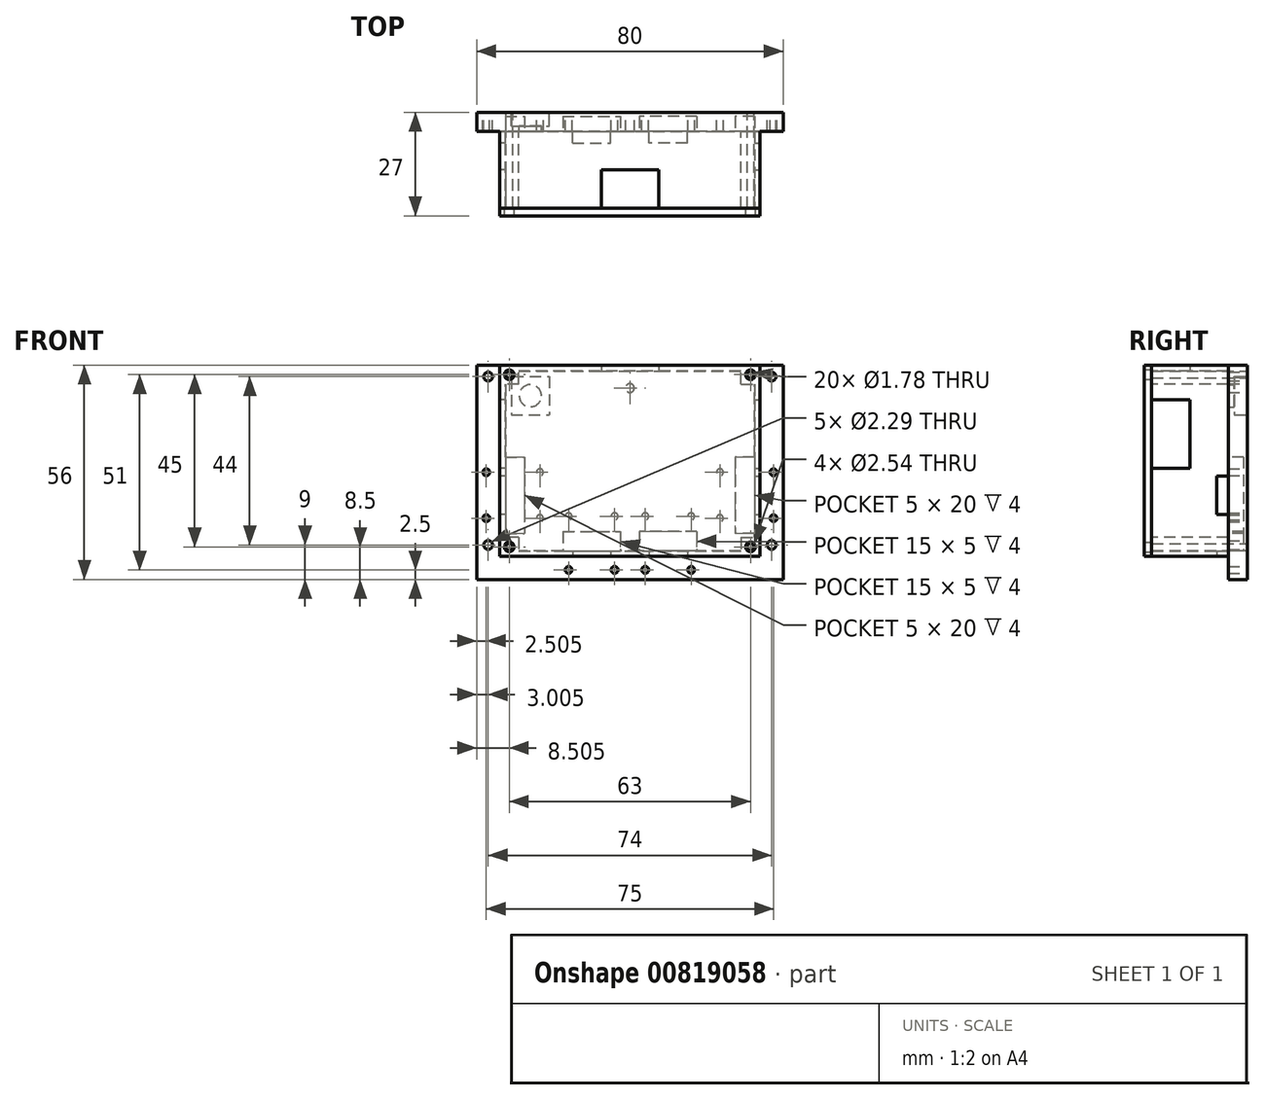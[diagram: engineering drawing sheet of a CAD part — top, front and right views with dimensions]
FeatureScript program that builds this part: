
annotation { "Feature Type Name" : "Feature", "Feature Type Description" : "" }
export const myFeature = defineFeature(function(context is Context, id is Id, definition is map)
    precondition{}
    {
        {
            var Q0;
            Q0=qCreatedBy(makeId("Front.planeOp"),FACE);
            var sketch = newSketch(context, id + "F0", { "sketchPlane" : qUnion([Q0])});
            skCircle(sketch, "E0", {"center": v(-19.88, 15) * mm, "radius": 0.89 * mm});
            skCircle(sketch, "E1", {"center": v(-25.88, -10.5) * mm, "radius": 0.89 * mm});
            skCircle(sketch, "E2", {"center": v(-11.88, -10.5) * mm, "radius": 0.89 * mm});
            skCircle(sketch, "E3", {"center": v(-11.88, -22.5) * mm, "radius": 0.89 * mm});
            skCircle(sketch, "E4", {"center": v(-25.88, -22.5) * mm, "radius": 0.89 * mm});
            skCircle(sketch, "E5", {"center": v(-25.38, -29.5) * mm, "radius": 1.14 * mm});
            skLineSegment(sketch, "E6", {"start": v(51.62, 17.5) * mm, "end": v(-28.38, 17.5) * mm});
            skLineSegment(sketch, "E7", {"start": v(-28.37, 17.5) * mm, "end": v(-28.38, -32.5) * mm});
            skLineSegment(sketch, "E8", {"start": v(51.63, -32.5) * mm, "end": v(-28.38, -32.5) * mm});
            skLineSegment(sketch, "E9.bottom", {"start": v(-28.38, -32.5) * mm, "end": v(-22.38, -32.5) * mm, "construction": true});
            skLineSegment(sketch, "E9.top", {"start": v(-28.38, -26.5) * mm, "end": v(-22.38, -26.5) * mm, "construction": true});
            skLineSegment(sketch, "E9.left", {"start": v(-28.38, -32.5) * mm, "end": v(-28.38, -26.5) * mm, "construction": true});
            skLineSegment(sketch, "E9.right", {"start": v(-22.38, -32.5) * mm, "end": v(-22.38, -26.5) * mm, "construction": true});
            skLineSegment(sketch, "E10", {"start": v(-28.37, -26.5) * mm, "end": v(-22.38, -32.5) * mm});
            skLineSegment(sketch, "E11", {"start": v(-28.38, -32.5) * mm, "end": v(-22.38, -26.5) * mm});
            skPoint(sketch, "E12", {"position": v(-28.38, -7.5) * mm});
            skLineSegment(sketch, "E13", {"start": v(11.62, 17.5) * mm, "end": v(-19.88, 17.5) * mm, "construction": true});
            skLineSegment(sketch, "E14", {"start": v(-19.88, 17.5) * mm, "end": v(-19.88, 15) * mm});
            skLineSegment(sketch, "E15", {"start": v(-11.88, -10.5) * mm, "end": v(-11.88, -22.5) * mm, "construction": true});
            skPoint(sketch, "E16", {"position": v(-11.88, -16.5) * mm});
            skLineSegment(sketch, "E17", {"start": v(-11.88, -16.5) * mm, "end": v(-28.38, -16.5) * mm, "construction": true});
            skLineSegment(sketch, "E18", {"start": v(-25.88, -22.5) * mm, "end": v(-25.88, -10.5) * mm, "construction": true});
            skPoint(sketch, "E19", {"position": v(-25.88, -16.5) * mm});
            skPoint(sketch, "E20", {"position": v(-20.88, -16.5) * mm});
            skLineSegment(sketch, "E21", {"start": v(-20.88, -16.5) * mm, "end": v(-20.88, -6.5) * mm, "construction": true});
            skLineSegment(sketch, "E22", {"start": v(-20.88, -6.5) * mm, "end": v(-15.88, -6.5) * mm, "construction": true});
            skLineSegment(sketch, "E23", {"start": v(-15.88, -6.5) * mm, "end": v(-15.88, -26.5) * mm, "construction": true});
            skLineSegment(sketch, "E24.bottom", {"start": v(-20.88, -6.5) * mm, "end": v(-15.88, -6.5) * mm});
            skLineSegment(sketch, "E24.top", {"start": v(-20.88, -26.5) * mm, "end": v(-15.88, -26.5) * mm});
            skLineSegment(sketch, "E24.left", {"start": v(-20.88, -6.5) * mm, "end": v(-20.88, -26.5) * mm});
            skLineSegment(sketch, "E24.right", {"start": v(-15.88, -6.5) * mm, "end": v(-15.88, -26.5) * mm});
            skLineSegment(sketch, "E25", {"start": v(-25.88, -10.5) * mm, "end": v(-28.38, -10.5) * mm, "construction": true});
            skLineSegment(sketch, "E26", {"start": v(-20.88, -6.5) * mm, "end": v(-28.38, -6.5) * mm, "construction": true});
            skLineSegment(sketch, "E27", {"start": v(51.62, 17.5) * mm, "end": v(51.63, -32.5) * mm});
            skLineSegment(sketch, "E28", {"start": v(11.62, 27.5) * mm, "end": v(11.62, 17.5) * mm, "construction": true});
            skLineSegment(sketch, "E29.bottom", {"start": v(-28.38, 17.5) * mm, "end": v(-22.38, 17.5) * mm, "construction": true});
            skLineSegment(sketch, "E29.top", {"start": v(-28.38, 11.5) * mm, "end": v(-22.38, 11.5) * mm, "construction": true});
            skLineSegment(sketch, "E29.left", {"start": v(-28.38, 17.5) * mm, "end": v(-28.38, 11.5) * mm, "construction": true});
            skLineSegment(sketch, "E29.right", {"start": v(-22.38, 17.5) * mm, "end": v(-22.38, 11.5) * mm, "construction": true});
            skLineSegment(sketch, "E30", {"start": v(-28.38, 17.5) * mm, "end": v(-22.38, 11.5) * mm, "construction": true});
            skLineSegment(sketch, "E31", {"start": v(-28.38, 11.5) * mm, "end": v(-22.38, 17.5) * mm, "construction": true});
            skCircle(sketch, "E32", {"center": v(-25.38, 14.5) * mm, "radius": 1.14 * mm});
            skCircle(sketch, "E33.MirrorC", {"center": v(48.62, -29.5) * mm, "radius": 1.14 * mm});
            skCircle(sketch, "E34.MirrorC", {"center": v(49.13, -22.5) * mm, "radius": 0.89 * mm});
            skLineSegment(sketch, "E35.MirrorCS", {"start": v(39.13, -6.5) * mm, "end": v(39.13, -26.5) * mm});
            skLineSegment(sketch, "E36.MirrorCS", {"start": v(44.13, -6.5) * mm, "end": v(39.13, -6.5) * mm});
            skLineSegment(sketch, "E37.MirrorCS", {"start": v(44.13, -6.5) * mm, "end": v(44.13, -26.5) * mm});
            skPoint(sketch, "E38.MirrorP", {"position": v(44.13, -16.5) * mm});
            skLineSegment(sketch, "E39.MirrorCS", {"start": v(44.13, -6.5) * mm, "end": v(39.13, -6.5) * mm, "construction": true});
            skLineSegment(sketch, "E40.MirrorCS", {"start": v(35.12, -10.5) * mm, "end": v(35.12, -22.5) * mm, "construction": true});
            skLineSegment(sketch, "E41.MirrorCS", {"start": v(44.13, -26.5) * mm, "end": v(39.13, -26.5) * mm});
            skLineSegment(sketch, "E42.MirrorCS", {"start": v(44.13, -16.5) * mm, "end": v(44.13, -6.5) * mm, "construction": true});
            skCircle(sketch, "E43.MirrorC", {"center": v(35.12, -22.5) * mm, "radius": 0.89 * mm});
            skCircle(sketch, "E44.MirrorC", {"center": v(35.12, -10.5) * mm, "radius": 0.89 * mm});
            skPoint(sketch, "E45.MirrorP", {"position": v(49.13, -16.5) * mm});
            skPoint(sketch, "E46.MirrorP", {"position": v(35.12, -16.5) * mm});
            skCircle(sketch, "E47.MirrorC", {"center": v(49.13, -10.5) * mm, "radius": 0.89 * mm});
            skLineSegment(sketch, "E48.MirrorCS", {"start": v(49.12, -22.5) * mm, "end": v(49.12, -10.5) * mm, "construction": true});
            skLineSegment(sketch, "E49.MirrorCS", {"start": v(39.13, -6.5) * mm, "end": v(39.13, -26.5) * mm, "construction": true});
            skPoint(sketch, "E50.MirrorP", {"position": v(51.62, -7.5) * mm});
            skCircle(sketch, "E51.MirrorC", {"center": v(48.62, 14.5) * mm, "radius": 1.14 * mm});
            skCircle(sketch, "E52.MirrorC", {"center": v(43.12, 15) * mm, "radius": 0.89 * mm});
            skLineSegment(sketch, "E53", {"start": v(44.13, -26.5) * mm, "end": v(45.63, -26.5) * mm, "construction": true});
            skLineSegment(sketch, "E54", {"start": v(45.63, -26.5) * mm, "end": v(45.63, -32.5) * mm});
            skLineSegment(sketch, "E55", {"start": v(45.63, -26.5) * mm, "end": v(45.63, 17.5) * mm});
            skLineSegment(sketch, "E56", {"start": v(-20.88, -26.5) * mm, "end": v(-22.38, -26.5) * mm, "construction": true});
            skLineSegment(sketch, "E57.bottom", {"start": v(-22.38, 17.5) * mm, "end": v(45.62, 17.5) * mm});
            skLineSegment(sketch, "E57.top", {"start": v(-22.38, -32.5) * mm, "end": v(45.63, -32.5) * mm});
            skLineSegment(sketch, "E57.left", {"start": v(-22.38, 17.5) * mm, "end": v(-22.38, -32.5) * mm});
            skLineSegment(sketch, "E57.right", {"start": v(45.63, 17.5) * mm, "end": v(45.63, -32.5) * mm});
            skLineSegment(sketch, "E58", {"start": v(-19.88, 15) * mm, "end": v(-17.38, 15) * mm, "construction": true});
            skLineSegment(sketch, "E59", {"start": v(-17.38, 15) * mm, "end": v(-17.38, 12.5) * mm, "construction": true});
            skLineSegment(sketch, "E60.bottom", {"start": v(-17.38, 12.5) * mm, "end": v(-22.38, 12.5) * mm});
            skLineSegment(sketch, "E60.top", {"start": v(-17.38, 17.5) * mm, "end": v(-22.38, 17.5) * mm});
            skLineSegment(sketch, "E60.left", {"start": v(-17.38, 12.5) * mm, "end": v(-17.38, 17.5) * mm});
            skLineSegment(sketch, "E60.right", {"start": v(-22.38, 12.5) * mm, "end": v(-22.38, 17.5) * mm});
            skLineSegment(sketch, "E61", {"start": v(43.12, 15) * mm, "end": v(40.63, 15) * mm, "construction": true});
            skLineSegment(sketch, "E62", {"start": v(40.63, 15) * mm, "end": v(40.63, 12.5) * mm, "construction": true});
            skLineSegment(sketch, "E63.bottom", {"start": v(40.63, 12.5) * mm, "end": v(45.62, 12.5) * mm});
            skLineSegment(sketch, "E63.top", {"start": v(40.63, 17.5) * mm, "end": v(45.62, 17.5) * mm});
            skLineSegment(sketch, "E63.left", {"start": v(40.63, 12.5) * mm, "end": v(40.63, 17.5) * mm});
            skLineSegment(sketch, "E63.right", {"start": v(45.63, 12.5) * mm, "end": v(45.63, 17.5) * mm});
            skLineSegment(sketch, "E64", {"start": v(11.63, -32.5) * mm, "end": v(13.43, -32.5) * mm});
            skLineSegment(sketch, "E65", {"start": v(44.13, -16.5) * mm, "end": v(47.13, -16.5) * mm, "construction": true});
            skLineSegment(sketch, "E66.bottom", {"start": v(43.13, -11.5) * mm, "end": v(47.13, -11.5) * mm});
            skLineSegment(sketch, "E66.top", {"start": v(43.13, -21.5) * mm, "end": v(47.13, -21.5) * mm});
            skLineSegment(sketch, "E66.left", {"start": v(43.13, -11.5) * mm, "end": v(43.13, -21.5) * mm});
            skLineSegment(sketch, "E66.right", {"start": v(47.13, -11.5) * mm, "end": v(47.13, -21.5) * mm});
            skPoint(sketch, "E67", {"position": v(47.13, -16.5) * mm});
            skLineSegment(sketch, "E68.MirrorCS", {"start": v(-19.88, -21.5) * mm, "end": v(-23.88, -21.5) * mm});
            skLineSegment(sketch, "E69.MirrorCS", {"start": v(-19.87, -11.5) * mm, "end": v(-19.87, -21.5) * mm});
            skLineSegment(sketch, "E70.MirrorCS", {"start": v(-23.87, -11.5) * mm, "end": v(-23.87, -21.5) * mm});
            skLineSegment(sketch, "E71.MirrorCS", {"start": v(-19.88, -11.5) * mm, "end": v(-23.88, -11.5) * mm});
            skPoint(sketch, "E72", {"position": v(45.62, 27.5) * mm});
            skLineSegment(sketch, "E73.bottom", {"start": v(4.12, 17.5) * mm, "end": v(19.12, 17.5) * mm});
            skLineSegment(sketch, "E73.top", {"start": v(4.12, 13.5) * mm, "end": v(19.12, 13.5) * mm});
            skLineSegment(sketch, "E73.left", {"start": v(4.12, 17.5) * mm, "end": v(4.12, 13.5) * mm});
            skLineSegment(sketch, "E73.right", {"start": v(19.12, 17.5) * mm, "end": v(19.12, 13.5) * mm});
            skPoint(sketch, "E74", {"position": v(11.62, 17.5) * mm});
            skLineSegment(sketch, "E75", {"start": v(-22.38, 17.5) * mm, "end": v(-19.88, 17.5) * mm});
            skLineSegment(sketch, "E76", {"start": v(-5.88, -32.5) * mm, "end": v(-5.88, -31) * mm, "construction": true});
            skLineSegment(sketch, "E77.bottom", {"start": v(-5.88, -26) * mm, "end": v(9.12, -26) * mm});
            skLineSegment(sketch, "E77.top", {"start": v(-5.88, -31) * mm, "end": v(9.12, -31) * mm});
            skLineSegment(sketch, "E77.left", {"start": v(-5.88, -26) * mm, "end": v(-5.88, -31) * mm});
            skLineSegment(sketch, "E77.right", {"start": v(9.12, -26) * mm, "end": v(9.12, -31) * mm});
            skPoint(sketch, "E78", {"position": v(1.62, -26) * mm});
            skLineSegment(sketch, "E79", {"start": v(1.62, -26) * mm, "end": v(1.62, -22) * mm, "construction": true});
            skLineSegment(sketch, "E80", {"start": v(-4.38, -22) * mm, "end": v(7.63, -22) * mm, "construction": true});
            skPoint(sketch, "E81", {"position": v(1.62, -22) * mm});
            skCircle(sketch, "E82", {"center": v(-4.38, -22) * mm, "radius": 0.89 * mm});
            skCircle(sketch, "E83", {"center": v(7.63, -22) * mm, "radius": 0.89 * mm});
            skLineSegment(sketch, "E84.bottom", {"start": v(-28.37, -32.5) * mm, "end": v(51.63, -32.5) * mm});
            skLineSegment(sketch, "E84.top", {"start": v(-28.37, -38.5) * mm, "end": v(51.63, -38.5) * mm});
            skLineSegment(sketch, "E84.left", {"start": v(-28.38, -32.5) * mm, "end": v(-28.38, -38.5) * mm});
            skLineSegment(sketch, "E84.right", {"start": v(51.63, -32.5) * mm, "end": v(51.63, -38.5) * mm});
            skLineSegment(sketch, "E85.bottom", {"start": v(-3.37, -31) * mm, "end": v(6.63, -31) * mm});
            skLineSegment(sketch, "E85.top", {"start": v(-3.38, -34) * mm, "end": v(6.63, -34) * mm});
            skLineSegment(sketch, "E85.left", {"start": v(-3.38, -31) * mm, "end": v(-3.38, -34) * mm});
            skLineSegment(sketch, "E85.right", {"start": v(6.63, -31) * mm, "end": v(6.63, -34) * mm});
            skPoint(sketch, "E86", {"position": v(1.63, -31) * mm});
            skPoint(sketch, "E87", {"position": v(1.62, -31) * mm});
            skLineSegment(sketch, "E88", {"start": v(1.63, -31) * mm, "end": v(1.63, -38.5) * mm, "construction": true});
            skLineSegment(sketch, "E89", {"start": v(1.63, -38.5) * mm, "end": v(1.63, -36) * mm, "construction": true});
            skLineSegment(sketch, "E90", {"start": v(-4.38, -36) * mm, "end": v(7.63, -36) * mm, "construction": true});
            skPoint(sketch, "E91", {"position": v(1.62, -36) * mm});
            skCircle(sketch, "E92", {"center": v(-4.38, -36) * mm, "radius": 0.89 * mm});
            skCircle(sketch, "E93", {"center": v(7.63, -36) * mm, "radius": 0.89 * mm});
            skCircle(sketch, "E94.MirrorC", {"center": v(15.62, -36) * mm, "radius": 0.89 * mm});
            skCircle(sketch, "E95.MirrorC", {"center": v(27.63, -36) * mm, "radius": 0.89 * mm});
            skLineSegment(sketch, "E96.MirrorCS", {"start": v(21.62, -38.5) * mm, "end": v(21.62, -36) * mm, "construction": true});
            skLineSegment(sketch, "E97.MirrorCS", {"start": v(26.62, -31) * mm, "end": v(26.62, -34) * mm});
            skLineSegment(sketch, "E98.MirrorCS", {"start": v(29.12, -32.5) * mm, "end": v(29.12, -31) * mm, "construction": true});
            skLineSegment(sketch, "E99.MirrorCS", {"start": v(29.12, -31) * mm, "end": v(14.12, -31) * mm});
            skPoint(sketch, "E100.MirrorP", {"position": v(21.62, -31) * mm});
            skLineSegment(sketch, "E101.MirrorCS", {"start": v(11.62, -32.5) * mm, "end": v(9.82, -32.5) * mm});
            skCircle(sketch, "E102.MirrorC", {"center": v(27.63, -22) * mm, "radius": 0.89 * mm});
            skCircle(sketch, "E103.MirrorC", {"center": v(15.62, -22) * mm, "radius": 0.89 * mm});
            skPoint(sketch, "E104.MirrorP", {"position": v(21.62, -36) * mm});
            skPoint(sketch, "E105.MirrorP", {"position": v(21.63, -31) * mm});
            skPoint(sketch, "E106.MirrorP", {"position": v(21.63, -26) * mm});
            skLineSegment(sketch, "E107.MirrorCS", {"start": v(21.63, -26) * mm, "end": v(21.63, -22) * mm, "construction": true});
            skLineSegment(sketch, "E108.MirrorCS", {"start": v(29.12, -26) * mm, "end": v(29.12, -31) * mm});
            skLineSegment(sketch, "E109.MirrorCS", {"start": v(27.63, -36) * mm, "end": v(15.62, -36) * mm, "construction": true});
            skLineSegment(sketch, "E110.MirrorCS", {"start": v(26.62, -34) * mm, "end": v(16.62, -34) * mm});
            skLineSegment(sketch, "E111.MirrorCS", {"start": v(21.62, -31) * mm, "end": v(21.62, -38.5) * mm, "construction": true});
            skLineSegment(sketch, "E112.MirrorCS", {"start": v(27.63, -22) * mm, "end": v(15.62, -22) * mm, "construction": true});
            skLineSegment(sketch, "E113.MirrorCS", {"start": v(29.12, -26) * mm, "end": v(14.12, -26) * mm});
            skLineSegment(sketch, "E114.MirrorCS", {"start": v(16.62, -31) * mm, "end": v(16.62, -34) * mm});
            skPoint(sketch, "E115.MirrorP", {"position": v(21.63, -22) * mm});
            skLineSegment(sketch, "E116.MirrorCS", {"start": v(26.62, -31) * mm, "end": v(16.62, -31) * mm});
            skLineSegment(sketch, "E117.MirrorCS", {"start": v(14.12, -26) * mm, "end": v(14.12, -31) * mm});
            skLineSegment(sketch, "E118", {"start": v(-28.38, -7.5) * mm, "end": v(51.62, -7.5) * mm, "construction": true});
            skCircle(sketch, "E119.MirrorC", {"center": v(43.13, -30) * mm, "radius": 0.89 * mm});
            skLineSegment(sketch, "E120.MirrorCS", {"start": v(40.63, -27.5) * mm, "end": v(45.63, -27.5) * mm});
            skLineSegment(sketch, "E121.MirrorCS", {"start": v(45.63, -27.5) * mm, "end": v(45.63, -32.5) * mm});
            skLineSegment(sketch, "E122.MirrorCS", {"start": v(40.63, -27.5) * mm, "end": v(40.63, -32.5) * mm});
            skLineSegment(sketch, "E123.MirrorCS", {"start": v(40.63, -32.5) * mm, "end": v(45.62, -32.5) * mm});
            skLineSegment(sketch, "E124.MirrorCS", {"start": v(40.63, -30) * mm, "end": v(40.63, -27.5) * mm, "construction": true});
            skLineSegment(sketch, "E125.MirrorCS", {"start": v(43.13, -30) * mm, "end": v(40.63, -30) * mm, "construction": true});
            skLineSegment(sketch, "E126.MirrorCS", {"start": v(-17.37, -27.5) * mm, "end": v(-17.37, -32.5) * mm});
            skLineSegment(sketch, "E127.MirrorCS", {"start": v(-19.88, -30) * mm, "end": v(-17.37, -30) * mm, "construction": true});
            skLineSegment(sketch, "E128.MirrorCS", {"start": v(-17.37, -30) * mm, "end": v(-17.37, -27.5) * mm, "construction": true});
            skLineSegment(sketch, "E129.MirrorCS", {"start": v(-17.38, -27.5) * mm, "end": v(-22.37, -27.5) * mm});
            skCircle(sketch, "E130.MirrorC", {"center": v(-19.88, -30) * mm, "radius": 0.89 * mm});
            skLineSegment(sketch, "E131.MirrorCS", {"start": v(-17.37, -32.5) * mm, "end": v(-22.38, -32.5) * mm});
            skLineSegment(sketch, "E132.MirrorCS", {"start": v(-22.38, -32.5) * mm, "end": v(-19.88, -32.5) * mm});
            skLineSegment(sketch, "E133.MirrorCS", {"start": v(-19.88, -32.5) * mm, "end": v(-19.88, -30) * mm});
            skLineSegment(sketch, "E134.MirrorCS", {"start": v(-22.38, -27.5) * mm, "end": v(-22.38, -32.5) * mm});
            skLineSegment(sketch, "E135.bottom", {"start": v(41.62, 8.5) * mm, "end": v(45.62, 8.5) * mm});
            skLineSegment(sketch, "E135.top", {"start": v(41.62, -9.5) * mm, "end": v(45.62, -9.5) * mm});
            skLineSegment(sketch, "E135.left", {"start": v(41.62, 8.5) * mm, "end": v(41.62, -9.5) * mm});
            skLineSegment(sketch, "E135.right", {"start": v(45.62, 8.5) * mm, "end": v(45.62, -9.5) * mm});
            skPoint(sketch, "E136", {"position": v(45.62, -0.5) * mm});
            skPoint(sketch, "E137.MirrorP", {"position": v(-22.38, -0.5) * mm});
            skLineSegment(sketch, "E138.MirrorCS", {"start": v(-22.38, 8.5) * mm, "end": v(-22.38, -9.5) * mm});
            skLineSegment(sketch, "E139.MirrorCS", {"start": v(-18.38, 8.5) * mm, "end": v(-18.38, -9.5) * mm});
            skLineSegment(sketch, "E140.MirrorCS", {"start": v(-18.38, 8.5) * mm, "end": v(-22.38, 8.5) * mm});
            skLineSegment(sketch, "E141.MirrorCS", {"start": v(-18.38, -9.5) * mm, "end": v(-22.38, -9.5) * mm});
            skCircle(sketch, "E142", {"center": v(-14.38, 9.5) * mm, "radius": 2.9 * mm, "construction": true});
            skLineSegment(sketch, "E143", {"start": v(-14.38, 9.5) * mm, "end": v(-14.38, 14.5) * mm, "construction": true});
            skLineSegment(sketch, "E144", {"start": v(-14.38, 14.5) * mm, "end": v(-19.38, 14.5) * mm, "construction": true});
            skLineSegment(sketch, "E145.bottom", {"start": v(-19.38, 14.5) * mm, "end": v(-9.38, 14.5) * mm});
            skLineSegment(sketch, "E145.top", {"start": v(-19.38, 4.5) * mm, "end": v(-9.38, 4.5) * mm});
            skLineSegment(sketch, "E145.left", {"start": v(-19.38, 14.5) * mm, "end": v(-19.38, 4.5) * mm});
            skLineSegment(sketch, "E145.right", {"start": v(-9.38, 14.5) * mm, "end": v(-9.38, 4.5) * mm});
            skLineSegment(sketch, "E146", {"start": v(45.62, -0.5) * mm, "end": v(45.62, 17.5) * mm, "construction": true});
            skLineSegment(sketch, "E147", {"start": v(-22.38, 9.5) * mm, "end": v(-14.38, 9.5) * mm, "construction": true});
            skLineSegment(sketch, "E148", {"start": v(-14.38, 17.5) * mm, "end": v(-14.38, 9.5) * mm, "construction": true});
            skLineSegment(sketch, "E149", {"start": v(11.62, 17.5) * mm, "end": v(11.62, 11.5) * mm, "construction": true});
            skCircle(sketch, "E150", {"center": v(11.62, 11.5) * mm, "radius": 1.14 * mm});
            skSolve(sketch);
        }
        {
            var Q0;
            Q0=qCreatedBy(makeId("Front.planeOp"),FACE);
            var sketch = newSketch(context, id + "F1", { "sketchPlane" : qUnion([Q0])});
            skLineSegment(sketch, "E151.0", {"start": v(51.62, 17.5) * mm, "end": v(-28.38, 17.5) * mm});
            skLineSegment(sketch, "E151.1", {"start": v(-28.37, 17.5) * mm, "end": v(-28.38, -32.5) * mm});
            skLineSegment(sketch, "E151.2", {"start": v(51.62, 17.5) * mm, "end": v(51.63, -32.5) * mm});
            skLineSegment(sketch, "E152.0", {"start": v(-28.38, -32.5) * mm, "end": v(-28.38, -38.5) * mm});
            skLineSegment(sketch, "E152.1", {"start": v(-28.37, -38.5) * mm, "end": v(51.63, -38.5) * mm});
            skLineSegment(sketch, "E152.2", {"start": v(51.63, -32.5) * mm, "end": v(51.63, -38.5) * mm});
            skSolve(sketch);
        }
        {
            var Q0;
            Q0=qCreatedBy(makeId("Front.planeOp"),FACE);
            var sketch = newSketch(context, id + "F2", { "sketchPlane" : qUnion([Q0])});
            skLineSegment(sketch, "E153.4", {"start": v(-20.88, -6.5) * mm, "end": v(-15.88, -6.5) * mm});
            skLineSegment(sketch, "E153.5", {"start": v(-20.88, -6.5) * mm, "end": v(-20.88, -26.5) * mm});
            skLineSegment(sketch, "E153.6", {"start": v(-15.88, -6.5) * mm, "end": v(-15.88, -26.5) * mm});
            skLineSegment(sketch, "E153.7", {"start": v(-20.88, -26.5) * mm, "end": v(-15.88, -26.5) * mm});
            skLineSegment(sketch, "E154.5", {"start": v(44.13, -6.5) * mm, "end": v(44.13, -26.5) * mm});
            skLineSegment(sketch, "E154.6", {"start": v(44.13, -6.5) * mm, "end": v(39.13, -6.5) * mm});
            skLineSegment(sketch, "E154.7", {"start": v(39.13, -6.5) * mm, "end": v(39.13, -26.5) * mm});
            skLineSegment(sketch, "E154.8", {"start": v(44.13, -26.5) * mm, "end": v(39.13, -26.5) * mm});
            skLineSegment(sketch, "E155.0", {"start": v(-5.88, -26) * mm, "end": v(9.12, -26) * mm});
            skLineSegment(sketch, "E155.1", {"start": v(-5.88, -26) * mm, "end": v(-5.88, -31) * mm});
            skLineSegment(sketch, "E155.2", {"start": v(-5.88, -31) * mm, "end": v(9.12, -31) * mm});
            skLineSegment(sketch, "E155.3", {"start": v(9.12, -26) * mm, "end": v(9.12, -31) * mm});
            skLineSegment(sketch, "E156.0", {"start": v(29.12, -26) * mm, "end": v(14.12, -26) * mm});
            skLineSegment(sketch, "E156.1", {"start": v(14.12, -26) * mm, "end": v(14.12, -31) * mm});
            skLineSegment(sketch, "E156.2", {"start": v(29.12, -31) * mm, "end": v(14.12, -31) * mm});
            skLineSegment(sketch, "E156.3", {"start": v(29.12, -26) * mm, "end": v(29.12, -31) * mm});
            skSolve(sketch);
        }
        {
            var Q0;
            Q0=qCreatedBy(makeId("Front.planeOp"),FACE);
            var sketch = newSketch(context, id + "F3", { "sketchPlane" : qUnion([Q0])});
            skCircle(sketch, "E157.10", {"center": v(-11.88, -10.5) * mm, "radius": 0.89 * mm});
            skCircle(sketch, "E157.11", {"center": v(-25.88, -10.5) * mm, "radius": 0.89 * mm});
            skCircle(sketch, "E157.12", {"center": v(-25.88, -22.5) * mm, "radius": 0.89 * mm});
            skCircle(sketch, "E157.13", {"center": v(-11.88, -22.5) * mm, "radius": 0.89 * mm});
            skCircle(sketch, "E157.22", {"center": v(-25.38, -29.5) * mm, "radius": 1.14 * mm});
            skCircle(sketch, "E158.0", {"center": v(-25.38, 14.5) * mm, "radius": 1.14 * mm});
            skCircle(sketch, "E158.4", {"center": v(48.62, 14.5) * mm, "radius": 1.14 * mm});
            skCircle(sketch, "E158.5", {"center": v(35.12, -10.5) * mm, "radius": 0.89 * mm});
            skCircle(sketch, "E158.6", {"center": v(35.12, -22.5) * mm, "radius": 0.89 * mm});
            skCircle(sketch, "E158.7", {"center": v(49.13, -10.5) * mm, "radius": 0.89 * mm});
            skCircle(sketch, "E158.8", {"center": v(49.13, -22.5) * mm, "radius": 0.89 * mm});
            skCircle(sketch, "E158.9", {"center": v(48.62, -29.5) * mm, "radius": 1.14 * mm});
            skCircle(sketch, "E159.0", {"center": v(-19.88, 15) * mm, "radius": 0.89 * mm});
            skCircle(sketch, "E159.1", {"center": v(43.12, 15) * mm, "radius": 0.89 * mm});
            skCircle(sketch, "E160.0", {"center": v(-19.88, -30) * mm, "radius": 0.89 * mm});
            skCircle(sketch, "E160.1", {"center": v(-4.38, -22) * mm, "radius": 0.89 * mm});
            skCircle(sketch, "E160.2", {"center": v(7.63, -22) * mm, "radius": 0.89 * mm});
            skCircle(sketch, "E160.3", {"center": v(-4.38, -36) * mm, "radius": 0.89 * mm});
            skCircle(sketch, "E160.4", {"center": v(7.63, -36) * mm, "radius": 0.89 * mm});
            skCircle(sketch, "E160.5", {"center": v(15.62, -22) * mm, "radius": 0.89 * mm});
            skCircle(sketch, "E160.6", {"center": v(27.63, -22) * mm, "radius": 0.89 * mm});
            skCircle(sketch, "E160.7", {"center": v(27.63, -36) * mm, "radius": 0.89 * mm});
            skCircle(sketch, "E160.8", {"center": v(15.62, -36) * mm, "radius": 0.89 * mm});
            skCircle(sketch, "E161.0", {"center": v(43.13, -30) * mm, "radius": 0.89 * mm});
            skCircle(sketch, "E162.0", {"center": v(-14.38, 9.5) * mm, "radius": 2.9 * mm});
            skCircle(sketch, "E163.0", {"center": v(11.62, 11.5) * mm, "radius": 1.14 * mm});
            skSolve(sketch);
        }
        {
            var Q0;
            Q0=qSketchRegion(id+"F1",true);
            extrude(context, id + "F4", {"entities" : qUnion([Q0]), "depth" : 5 * mm, "offsetDistance" : 25 * mm});
        }
        {
            var Q0;
            Q0=qCreatedBy(makeId("Front.planeOp"),FACE);
            var sketch = newSketch(context, id + "F5", { "sketchPlane" : qUnion([Q0])});
            skLineSegment(sketch, "E164.0", {"start": v(-22.38, 17.5) * mm, "end": v(-22.38, -32.5) * mm});
            skLineSegment(sketch, "E164.1", {"start": v(-22.38, 17.5) * mm, "end": v(45.62, 17.5) * mm});
            skLineSegment(sketch, "E164.2", {"start": v(45.63, -26.5) * mm, "end": v(45.63, 17.5) * mm});
            skLineSegment(sketch, "E164.4", {"start": v(45.63, 17.5) * mm, "end": v(45.63, -32.5) * mm});
            skLineSegment(sketch, "E165.0", {"start": v(-22.38, -32.5) * mm, "end": v(45.63, -32.5) * mm});
            skLineSegment(sketch, "E166.0", {"start": v(-20.88, 16) * mm, "end": v(44.13, 16) * mm});
            skLineSegment(sketch, "E166.1", {"start": v(-20.88, 16) * mm, "end": v(-20.88, -31) * mm});
            skLineSegment(sketch, "E166.2", {"start": v(-20.88, -31) * mm, "end": v(44.13, -31) * mm});
            skLineSegment(sketch, "E166.3", {"start": v(44.13, 16) * mm, "end": v(44.13, -31) * mm});
            skSolve(sketch);
        }
        {
            var Q0;
            Q0=qCreatedBy(makeId("Front.planeOp"),FACE);
            var sketch = newSketch(context, id + "F6", { "sketchPlane" : qUnion([Q0])});
            skLineSegment(sketch, "E167.0", {"start": v(-17.38, 12.5) * mm, "end": v(-17.38, 17.5) * mm});
            skLineSegment(sketch, "E167.1", {"start": v(-17.38, 12.5) * mm, "end": v(-22.38, 12.5) * mm});
            skLineSegment(sketch, "E167.2", {"start": v(-17.38, 17.5) * mm, "end": v(-22.38, 17.5) * mm});
            skLineSegment(sketch, "E167.3", {"start": v(-22.38, 12.5) * mm, "end": v(-22.38, 17.5) * mm});
            skLineSegment(sketch, "E168.0", {"start": v(40.63, 12.5) * mm, "end": v(45.62, 12.5) * mm});
            skLineSegment(sketch, "E168.1", {"start": v(40.63, 12.5) * mm, "end": v(40.63, 17.5) * mm});
            skLineSegment(sketch, "E168.2", {"start": v(45.63, 12.5) * mm, "end": v(45.63, 17.5) * mm});
            skLineSegment(sketch, "E168.3", {"start": v(40.63, 17.5) * mm, "end": v(45.62, 17.5) * mm});
            skLineSegment(sketch, "E169.0", {"start": v(-17.38, -27.5) * mm, "end": v(-22.37, -27.5) * mm});
            skLineSegment(sketch, "E169.1", {"start": v(-17.37, -27.5) * mm, "end": v(-17.37, -32.5) * mm});
            skLineSegment(sketch, "E169.2", {"start": v(-17.37, -32.5) * mm, "end": v(-22.38, -32.5) * mm});
            skLineSegment(sketch, "E169.3", {"start": v(-22.38, -27.5) * mm, "end": v(-22.38, -32.5) * mm});
            skPoint(sketch, "E169.4", {"position": v(-19.87, -27.5) * mm});
            skLineSegment(sketch, "E170.0", {"start": v(40.63, -27.5) * mm, "end": v(45.63, -27.5) * mm});
            skLineSegment(sketch, "E170.1", {"start": v(40.63, -27.5) * mm, "end": v(40.63, -32.5) * mm});
            skLineSegment(sketch, "E170.2", {"start": v(45.63, -27.5) * mm, "end": v(45.63, -32.5) * mm});
            skLineSegment(sketch, "E170.3", {"start": v(40.63, -32.5) * mm, "end": v(45.62, -32.5) * mm});
            skSolve(sketch);
        }
        {
            var Q0;
            Q0=qSketchRegion(id+"F5",true);
            extrude(context, id + "F7", {"entities" : qUnion([Q0]), "operationType" : NewBodyOperationType.ADD, "depth" : 25 * mm, "offsetDistance" : 25 * mm});
        }
        {
            var Q0;
            {var subQ0=sQuery(id+"F1.wireOp",EDGE,"E152.2");var subQ1=sQuery(id+"F1.wireOp",EDGE,"E151.2");var subQ2=sQuery(id+"F1.wireOp",EDGE,"E152.0");var subQ3=sQuery(id+"F1.wireOp",EDGE,"E151.1");var subQ4=sQuery(id+"F1.wireOp",EDGE,"E152.1");var subQ5=sQuery(id+"F1.wireOp",EDGE,"E151.0");Q0=makeQuery(id+"F7.boolean.opBoolean","SPLIT",FACE,{"disambiguationData":[TD([makeQuery(id+"F4.opExtrude","SWEPT_FACE",FACE,{"disambiguationData":[OSD([subQ5])]})])],"derivedFrom":makeQuery(id+"F4.opExtrude","CAP_FACE",FACE,{"disambiguationData":[OSD([subQ5,subQ3,subQ1,subQ2,subQ4,subQ0])],"isStart":false})});}
            var sketch = newSketch(context, id + "F8", { "sketchPlane" : qUnion([Q0])});
            skLineSegment(sketch, "E171.0", {"start": v(-20.88, -6.5) * mm, "end": v(-15.88, -6.5) * mm});
            skLineSegment(sketch, "E171.1", {"start": v(-15.88, -6.5) * mm, "end": v(-15.88, -26.5) * mm});
            skLineSegment(sketch, "E171.2", {"start": v(-20.88, -6.5) * mm, "end": v(-20.88, -26.5) * mm});
            skLineSegment(sketch, "E171.3", {"start": v(-20.88, -26.5) * mm, "end": v(-15.88, -26.5) * mm});
            skLineSegment(sketch, "E171.4", {"start": v(-5.88, -26) * mm, "end": v(9.12, -26) * mm});
            skLineSegment(sketch, "E171.5", {"start": v(-5.88, -26) * mm, "end": v(-5.88, -31) * mm});
            skLineSegment(sketch, "E171.6", {"start": v(-5.88, -31) * mm, "end": v(9.12, -31) * mm});
            skLineSegment(sketch, "E171.7", {"start": v(9.12, -26) * mm, "end": v(9.12, -31) * mm});
            skLineSegment(sketch, "E171.8", {"start": v(29.12, -26) * mm, "end": v(14.12, -26) * mm});
            skLineSegment(sketch, "E171.9", {"start": v(14.12, -26) * mm, "end": v(14.12, -31) * mm});
            skLineSegment(sketch, "E171.10", {"start": v(29.12, -31) * mm, "end": v(14.12, -31) * mm});
            skLineSegment(sketch, "E171.11", {"start": v(29.12, -26) * mm, "end": v(29.12, -31) * mm});
            skLineSegment(sketch, "E171.12", {"start": v(39.13, -6.5) * mm, "end": v(39.13, -26.5) * mm});
            skLineSegment(sketch, "E171.13", {"start": v(44.13, -6.5) * mm, "end": v(39.13, -6.5) * mm});
            skLineSegment(sketch, "E171.14", {"start": v(44.13, -26.5) * mm, "end": v(39.13, -26.5) * mm});
            skLineSegment(sketch, "E171.15", {"start": v(44.13, -6.5) * mm, "end": v(44.13, -26.5) * mm});
            skPoint(sketch, "E171.16", {"position": v(41.63, -6.5) * mm});
            skSolve(sketch);
        }
        {
            var Q0;
            Q0=qSketchRegion(id+"F8",true);
            extrude(context, id + "F9", {"entities" : qUnion([Q0]), "operationType" : NewBodyOperationType.REMOVE, "oppositeDirection" : true, "depth" : 4 * mm, "offsetDistance" : 25 * mm});
        }
        {
            var Q0;
            Q0=qSketchRegion(id+"F6",true);
            extrude(context, id + "F10", {"entities" : qUnion([Q0]), "operationType" : NewBodyOperationType.ADD, "depth" : 25 * mm, "offsetDistance" : 25 * mm});
        }
        {
            var Q0;
            {var subQ0=sQuery(id+"F1.wireOp",EDGE,"E152.2");var subQ1=sQuery(id+"F1.wireOp",EDGE,"E151.2");var subQ2=sQuery(id+"F1.wireOp",EDGE,"E152.0");var subQ3=sQuery(id+"F1.wireOp",EDGE,"E151.1");var subQ4=sQuery(id+"F1.wireOp",EDGE,"E152.1");var subQ5=sQuery(id+"F1.wireOp",EDGE,"E151.0");Q0=makeQuery(id+"F7.boolean.opBoolean","SPLIT",FACE,{"disambiguationData":[TD([makeQuery(id+"F4.opExtrude","SWEPT_FACE",FACE,{"disambiguationData":[OSD([subQ5])]})])],"derivedFrom":makeQuery(id+"F4.opExtrude","CAP_FACE",FACE,{"disambiguationData":[OSD([subQ5,subQ3,subQ1,subQ2,subQ4,subQ0])],"isStart":false})});}
            var sketch = newSketch(context, id + "F11", { "sketchPlane" : qUnion([Q0])});
            skLineSegment(sketch, "E172.0", {"start": v(-19.88, -11.5) * mm, "end": v(-23.88, -11.5) * mm});
            skLineSegment(sketch, "E172.1", {"start": v(-23.87, -11.5) * mm, "end": v(-23.87, -21.5) * mm});
            skLineSegment(sketch, "E172.2", {"start": v(-19.87, -11.5) * mm, "end": v(-19.87, -21.5) * mm});
            skLineSegment(sketch, "E172.3", {"start": v(-19.88, -21.5) * mm, "end": v(-23.88, -21.5) * mm});
            skLineSegment(sketch, "E172.4", {"start": v(43.13, -11.5) * mm, "end": v(47.13, -11.5) * mm});
            skLineSegment(sketch, "E172.5", {"start": v(43.13, -11.5) * mm, "end": v(43.13, -21.5) * mm});
            skLineSegment(sketch, "E172.6", {"start": v(47.13, -11.5) * mm, "end": v(47.13, -21.5) * mm});
            skLineSegment(sketch, "E172.7", {"start": v(43.13, -21.5) * mm, "end": v(47.13, -21.5) * mm});
            skLineSegment(sketch, "E173.0", {"start": v(26.62, -34) * mm, "end": v(16.62, -34) * mm});
            skLineSegment(sketch, "E173.1", {"start": v(16.62, -31) * mm, "end": v(16.62, -34) * mm});
            skLineSegment(sketch, "E173.2", {"start": v(26.62, -31) * mm, "end": v(26.62, -34) * mm});
            skLineSegment(sketch, "E174.0", {"start": v(26.62, -31) * mm, "end": v(16.62, -31) * mm});
            skLineSegment(sketch, "E175.0", {"start": v(6.63, -31) * mm, "end": v(6.63, -34) * mm});
            skLineSegment(sketch, "E175.1", {"start": v(-3.38, -31) * mm, "end": v(-3.38, -34) * mm});
            skLineSegment(sketch, "E175.2", {"start": v(-3.38, -34) * mm, "end": v(6.63, -34) * mm});
            skLineSegment(sketch, "E175.3", {"start": v(-3.37, -31) * mm, "end": v(6.63, -31) * mm});
            skSolve(sketch);
        }
        {
            var Q0;
            Q0=qSketchRegion(id+"F11",true);
            extrude(context, id + "F12", {"entities" : qUnion([Q0]), "operationType" : NewBodyOperationType.REMOVE, "depth" : 3 * mm, "offsetDistance" : 25 * mm});
        }
        {
            var Q0;
            Q0=makeQuery(id+"F10.boolean.opBoolean","MERGE",FACE,{"derivedFrom":[makeQuery(id+"F7.opExtrude","CAP_FACE",FACE,{"disambiguationData":[OSD([sQuery(id+"F5.wireOp",EDGE,"E164.0"),sQuery(id+"F5.wireOp",EDGE,"E164.1"),sQuery(id+"F5.wireOp",EDGE,"E164.4"),sQuery(id+"F5.wireOp",EDGE,"E165.0"),sQuery(id+"F5.wireOp",EDGE,"E166.0"),sQuery(id+"F5.wireOp",EDGE,"E166.1"),sQuery(id+"F5.wireOp",EDGE,"E166.2"),sQuery(id+"F5.wireOp",EDGE,"E166.3")])],"isStart":false}),makeQuery(id+"F10.opExtrude","CAP_FACE",FACE,{"disambiguationData":[OSD([sQuery(id+"F6.wireOp",EDGE,"E167.0"),sQuery(id+"F6.wireOp",EDGE,"E167.1"),sQuery(id+"F6.wireOp",EDGE,"E167.2"),sQuery(id+"F6.wireOp",EDGE,"E167.3")])],"isStart":false}),makeQuery(id+"F10.opExtrude","CAP_FACE",FACE,{"disambiguationData":[OSD([sQuery(id+"F6.wireOp",EDGE,"E168.0"),sQuery(id+"F6.wireOp",EDGE,"E168.1"),sQuery(id+"F6.wireOp",EDGE,"E168.2"),sQuery(id+"F6.wireOp",EDGE,"E168.3")])],"isStart":false}),makeQuery(id+"F10.opExtrude","CAP_FACE",FACE,{"disambiguationData":[OSD([sQuery(id+"F6.wireOp",EDGE,"E169.0"),sQuery(id+"F6.wireOp",EDGE,"E169.1"),sQuery(id+"F6.wireOp",EDGE,"E169.2"),sQuery(id+"F6.wireOp",EDGE,"E169.3")])],"isStart":false}),makeQuery(id+"F10.opExtrude","CAP_FACE",FACE,{"disambiguationData":[OSD([sQuery(id+"F6.wireOp",EDGE,"E170.0"),sQuery(id+"F6.wireOp",EDGE,"E170.1"),sQuery(id+"F6.wireOp",EDGE,"E170.2"),sQuery(id+"F6.wireOp",EDGE,"E170.3")])],"isStart":false})]});
            var sketch = newSketch(context, id + "F13", { "sketchPlane" : qUnion([Q0])});
            skLineSegment(sketch, "E176.0", {"start": v(4.12, 13.5) * mm, "end": v(19.12, 13.5) * mm});
            skLineSegment(sketch, "E176.1", {"start": v(4.12, 17.5) * mm, "end": v(4.12, 13.5) * mm});
            skLineSegment(sketch, "E176.2", {"start": v(19.12, 17.5) * mm, "end": v(19.12, 13.5) * mm});
            skLineSegment(sketch, "E176.3", {"start": v(4.12, 17.5) * mm, "end": v(19.12, 17.5) * mm});
            skLineSegment(sketch, "E177.0", {"start": v(-18.38, 31.5) * mm, "end": v(-18.38, 23.5) * mm});
            skLineSegment(sketch, "E177.1", {"start": v(-18.37, 23.5) * mm, "end": v(-22.37, 23.5) * mm});
            skLineSegment(sketch, "E177.2", {"start": v(-18.37, 31.5) * mm, "end": v(-22.38, 31.5) * mm});
            skLineSegment(sketch, "E177.3", {"start": v(-22.38, 31.5) * mm, "end": v(-22.38, 23.5) * mm});
            skLineSegment(sketch, "E178.0", {"start": v(-18.38, 8.5) * mm, "end": v(-22.38, 8.5) * mm});
            skLineSegment(sketch, "E178.1", {"start": v(-18.38, 8.5) * mm, "end": v(-18.38, -9.5) * mm});
            skLineSegment(sketch, "E178.2", {"start": v(-18.38, -9.5) * mm, "end": v(-22.38, -9.5) * mm});
            skLineSegment(sketch, "E178.3", {"start": v(-22.38, 8.5) * mm, "end": v(-22.38, -9.5) * mm});
            skLineSegment(sketch, "E179.0", {"start": v(41.62, 23.5) * mm, "end": v(45.62, 23.5) * mm});
            skLineSegment(sketch, "E179.1", {"start": v(41.63, 31.5) * mm, "end": v(41.63, 23.5) * mm});
            skLineSegment(sketch, "E179.2", {"start": v(41.62, 31.5) * mm, "end": v(45.62, 31.5) * mm});
            skLineSegment(sketch, "E179.3", {"start": v(41.62, 8.5) * mm, "end": v(45.62, 8.5) * mm});
            skLineSegment(sketch, "E179.4", {"start": v(41.62, 8.5) * mm, "end": v(41.62, -9.5) * mm});
            skLineSegment(sketch, "E179.5", {"start": v(41.62, -9.5) * mm, "end": v(45.62, -9.5) * mm});
            skLineSegment(sketch, "E180.0", {"start": v(45.63, 31.5) * mm, "end": v(45.63, 23.5) * mm});
            skLineSegment(sketch, "E181.0", {"start": v(45.62, 8.5) * mm, "end": v(45.62, -9.5) * mm});
            skSolve(sketch);
        }
        {
            var Q0;
            Q0=qSketchRegion(id+"F13",true);
            extrude(context, id + "F14", {"entities" : qUnion([Q0]), "operationType" : NewBodyOperationType.REMOVE, "oppositeDirection" : true, "depth" : 10 * mm, "offsetDistance" : 25 * mm});
        }
        {
            var Q0;
            Q0=qSketchRegion(id+"F3",true);
            extrude(context, id + "F15", {"entities" : qUnion([Q0]), "operationType" : NewBodyOperationType.REMOVE, "endBound" : BoundingType.THROUGH_ALL, "depth" : 25 * mm, "offsetDistance" : 25 * mm});
        }
        {
            var Q0;
            Q0=qCreatedBy(makeId("Front.planeOp"),FACE);
            var sketch = newSketch(context, id + "F16", { "sketchPlane" : qUnion([Q0])});
            skLineSegment(sketch, "E182.0", {"start": v(-19.38, 14.5) * mm, "end": v(-9.38, 14.5) * mm});
            skLineSegment(sketch, "E182.1", {"start": v(-19.38, 14.5) * mm, "end": v(-19.38, 4.5) * mm});
            skLineSegment(sketch, "E182.2", {"start": v(-19.38, 4.5) * mm, "end": v(-9.38, 4.5) * mm});
            skLineSegment(sketch, "E182.3", {"start": v(-9.38, 14.5) * mm, "end": v(-9.38, 4.5) * mm});
            skSolve(sketch);
        }
        {
            var Q0;
            Q0=qSketchRegion(id+"F16",true);
            extrude(context, id + "F17", {"entities" : qUnion([Q0]), "operationType" : NewBodyOperationType.REMOVE, "depth" : 3.5 * mm, "offsetDistance" : 25 * mm});
        }
        {
            var Q0;
            {var subQ0=sQuery(id+"F5.wireOp",EDGE,"E166.0");var subQ1=sQuery(id+"F6.wireOp",EDGE,"E167.0");var subQ2=sQuery(id+"F5.wireOp",EDGE,"E164.1");var subQ3=sQuery(id+"F5.wireOp",EDGE,"E164.0");var subQ4=sQuery(id+"F6.wireOp",EDGE,"E167.1");var subQ5=sQuery(id+"F5.wireOp",EDGE,"E166.1");Q0=makeQuery(id+"F14.boolean.opBoolean","SPLIT",FACE,{"disambiguationData":[TD([makeQuery(id+"F10.opExtrude","SWEPT_FACE",FACE,{"disambiguationData":[OSD([subQ1])]})])],"derivedFrom":makeQuery(id+"F10.boolean.opBoolean","MERGE",FACE,{"derivedFrom":[makeQuery(id+"F7.opExtrude","CAP_FACE",FACE,{"disambiguationData":[OSD([subQ3,subQ2,sQuery(id+"F5.wireOp",EDGE,"E164.4"),sQuery(id+"F5.wireOp",EDGE,"E165.0"),subQ0,subQ5,sQuery(id+"F5.wireOp",EDGE,"E166.2"),sQuery(id+"F5.wireOp",EDGE,"E166.3")])],"isStart":false}),makeQuery(id+"F10.opExtrude","CAP_FACE",FACE,{"disambiguationData":[OSD([subQ1,subQ4,sQuery(id+"F6.wireOp",EDGE,"E167.2"),sQuery(id+"F6.wireOp",EDGE,"E167.3")])],"isStart":false}),makeQuery(id+"F10.opExtrude","CAP_FACE",FACE,{"disambiguationData":[OSD([sQuery(id+"F6.wireOp",EDGE,"E168.0"),sQuery(id+"F6.wireOp",EDGE,"E168.1"),sQuery(id+"F6.wireOp",EDGE,"E168.2"),sQuery(id+"F6.wireOp",EDGE,"E168.3")])],"isStart":false}),makeQuery(id+"F10.opExtrude","CAP_FACE",FACE,{"disambiguationData":[OSD([sQuery(id+"F6.wireOp",EDGE,"E169.0"),sQuery(id+"F6.wireOp",EDGE,"E169.1"),sQuery(id+"F6.wireOp",EDGE,"E169.2"),sQuery(id+"F6.wireOp",EDGE,"E169.3")])],"isStart":false}),makeQuery(id+"F10.opExtrude","CAP_FACE",FACE,{"disambiguationData":[OSD([sQuery(id+"F6.wireOp",EDGE,"E170.0"),sQuery(id+"F6.wireOp",EDGE,"E170.1"),sQuery(id+"F6.wireOp",EDGE,"E170.2"),sQuery(id+"F6.wireOp",EDGE,"E170.3")])],"isStart":false})]})});}
            var sketch = newSketch(context, id + "F18", { "sketchPlane" : qUnion([Q0])});
            skCircle(sketch, "E183.0", {"center": v(-19.88, 15) * mm, "radius": 0.89 * mm, "construction": true});
            skCircle(sketch, "E184", {"center": v(-19.88, 15) * mm, "radius": 1.27 * mm});
            skCircle(sketch, "E185.0", {"center": v(43.12, 15) * mm, "radius": 0.89 * mm, "construction": true});
            skCircle(sketch, "E186.0", {"center": v(43.13, -30) * mm, "radius": 0.89 * mm, "construction": true});
            skCircle(sketch, "E187.0", {"center": v(-19.88, -30) * mm, "radius": 0.89 * mm, "construction": true});
            skLineSegment(sketch, "E188.0", {"start": v(45.63, 17.5) * mm, "end": v(45.63, -32.5) * mm, "construction": true});
            skLineSegment(sketch, "E189.bottom", {"start": v(-22.38, 17.5) * mm, "end": v(45.63, 17.5) * mm});
            skLineSegment(sketch, "E189.top", {"start": v(-22.38, -32.5) * mm, "end": v(45.63, -32.5) * mm});
            skLineSegment(sketch, "E189.left", {"start": v(-22.38, 17.5) * mm, "end": v(-22.38, -32.5) * mm});
            skLineSegment(sketch, "E189.right", {"start": v(45.63, 17.5) * mm, "end": v(45.63, -32.5) * mm});
            skCircle(sketch, "E190", {"center": v(43.12, 15) * mm, "radius": 1.27 * mm});
            skCircle(sketch, "E191", {"center": v(-19.88, -30) * mm, "radius": 1.27 * mm});
            skCircle(sketch, "E192", {"center": v(43.13, -30) * mm, "radius": 1.27 * mm});
            skSolve(sketch);
        }
        {
            var Q0;
            Q0 = qSketchRegion(id + "F18", true);
            extrude(context, id + "F19", {"entities" : qUnion([Q0]), "depth" : 2 * mm, "offsetDistance" : 25 * mm});
        }
    });
